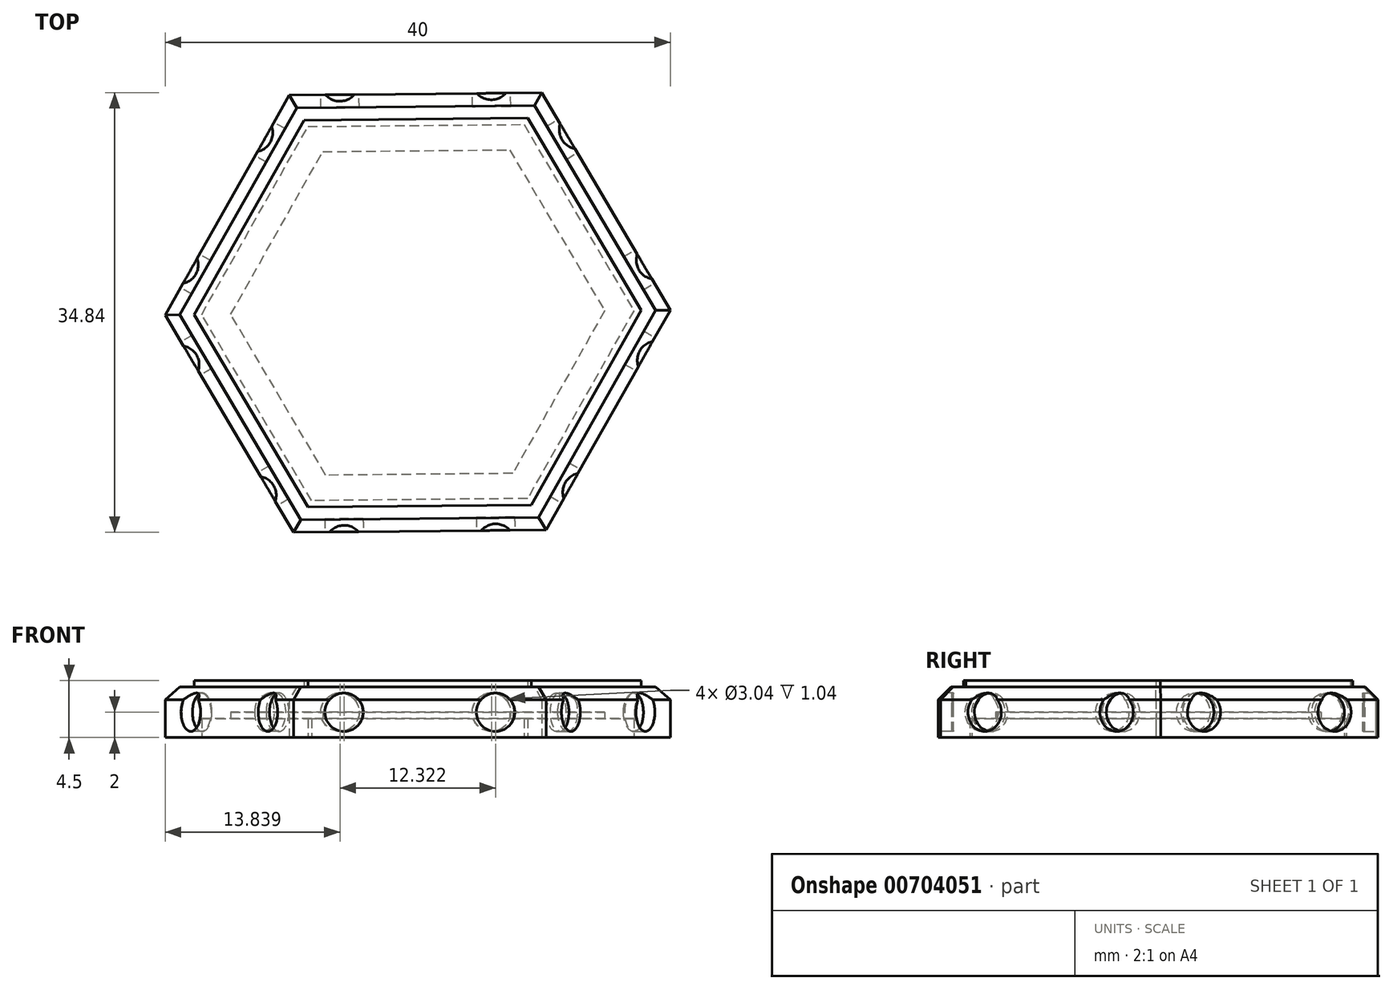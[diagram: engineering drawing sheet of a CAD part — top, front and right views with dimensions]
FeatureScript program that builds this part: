
annotation { "Feature Type Name" : "Feature", "Feature Type Description" : "" }
export const myFeature = defineFeature(function(context is Context, id is Id, definition is map)
    precondition{}
    {
        {
            var Q0;
            Q0=qCreatedBy(makeId("Top.planeOp"),FACE);
            var sketch = newSketch(context, id + "F0", { "sketchPlane" : qUnion([Q0])});
            skCircle(sketch, "E0.cCircle", {"center": v(0, 0) * mm, "radius": 15.32 * mm, "construction": true});
            skLineSegment(sketch, "E0.0", {"start": v(-17.69, -0.17) * mm, "end": v(-9, 15.23) * mm});
            skLineSegment(sketch, "E0.1", {"start": v(-9, 15.23) * mm, "end": v(8.7, 15.4) * mm});
            skLineSegment(sketch, "E0.2", {"start": v(8.7, 15.4) * mm, "end": v(17.69, 0.17) * mm});
            skLineSegment(sketch, "E0.3", {"start": v(17.69, 0.17) * mm, "end": v(9, -15.23) * mm});
            skLineSegment(sketch, "E0.4", {"start": v(9, -15.23) * mm, "end": v(-8.7, -15.4) * mm});
            skLineSegment(sketch, "E0.5", {"start": v(-8.7, -15.4) * mm, "end": v(-17.69, -0.17) * mm});
            skPoint(sketch, "E0.0.midPoint", {"position": v(-13.34, 7.53) * mm});
            skLineSegment(sketch, "E1.0", {"start": v(-9.83, -17.42) * mm, "end": v(-20, -0.2) * mm});
            skLineSegment(sketch, "E1.1", {"start": v(-10.17, 17.22) * mm, "end": v(9.83, 17.42) * mm});
            skLineSegment(sketch, "E1.2", {"start": v(9.83, 17.42) * mm, "end": v(20, 0.2) * mm});
            skLineSegment(sketch, "E1.3", {"start": v(-20, -0.2) * mm, "end": v(-10.17, 17.22) * mm});
            skLineSegment(sketch, "E1.4", {"start": v(20, 0.2) * mm, "end": v(10.17, -17.22) * mm});
            skLineSegment(sketch, "E1.5", {"start": v(10.17, -17.22) * mm, "end": v(-9.83, -17.42) * mm});
            skSolve(sketch);
        }
        {
            var Q0;
            Q0=makeQuery(id+"F0.imprint","IMPRINT",FACE,{"disambiguationData":[TD([[makeQuery(id+"F0.imprint","IMPRINT",EDGE,{"derivedFrom":sQuery(id+"F0.wireOp",EDGE,"E0.0")}),-1.0]])]});
            extrude(context, id + "F1", {"entities" : qUnion([Q0]), "depth" : 4.5 * mm, "offsetDistance" : 25 * mm});
        }
        {
            var Q0;
            Q0=makeQuery(id+"F0.imprint","IMPRINT",FACE,{"disambiguationData":[TD([[makeQuery(id+"F0.imprint","IMPRINT",EDGE,{"derivedFrom":sQuery(id+"F0.wireOp",EDGE,"E0.0")}),1.0]])]});
            extrude(context, id + "F2", {"entities" : qUnion([Q0]), "operationType" : NewBodyOperationType.ADD, "depth" : 4 * mm, "offsetDistance" : 25 * mm});
        }
        {
            var Q0;
            {var subQ0=sQuery(id+"F0.wireOp",EDGE,"E0.5");var subQ1=sQuery(id+"F0.wireOp",EDGE,"E0.4");var subQ2=sQuery(id+"F0.wireOp",EDGE,"E0.3");var subQ3=sQuery(id+"F0.wireOp",EDGE,"E0.2");var subQ4=sQuery(id+"F0.wireOp",EDGE,"E0.1");var subQ5=sQuery(id+"F0.wireOp",EDGE,"E0.0");Q0=makeQuery(id+"F2.boolean.opBoolean","MERGE",FACE,{"derivedFrom":[makeQuery(id+"F1.opExtrude","CAP_FACE",FACE,{"disambiguationData":[OSD([subQ5,subQ4,subQ3,subQ2,subQ1,subQ0])],"isStart":true}),makeQuery(id+"F2.opExtrude","CAP_FACE",FACE,{"disambiguationData":[OSD([subQ5,subQ4,subQ3,subQ2,subQ1,subQ0,sQuery(id+"F0.wireOp",EDGE,"E1.0"),sQuery(id+"F0.wireOp",EDGE,"E1.1"),sQuery(id+"F0.wireOp",EDGE,"E1.2"),sQuery(id+"F0.wireOp",EDGE,"E1.3"),sQuery(id+"F0.wireOp",EDGE,"E1.4"),sQuery(id+"F0.wireOp",EDGE,"E1.5")])],"isStart":true})]});}
            shell(context, id + "F3", {"entities" : qUnion([Q0]), "thickness" : 2.5 * mm});
        }
        {
            var Q0;
            Q0=makeQuery(id+"F2.opExtrude","SWEPT_FACE",FACE,{"disambiguationData":[OSD([sQuery(id+"F0.wireOp",EDGE,"E1.4")])]});
            var sketch = newSketch(context, id + "F4", { "sketchPlane" : qUnion([Q0])});
            skCircle(sketch, "E2", {"center": v(6, 2) * mm, "radius": 1.52 * mm});
            skCircle(sketch, "E3", {"center": v(-6, 2) * mm, "radius": 1.52 * mm});
            skSolve(sketch);
        }
        {
            var Q0;
            Q0=makeQuery(id+"F4.imprint","IMPRINT",FACE,{"disambiguationData":[TD([[makeQuery(id+"F4.imprint","IMPRINT",EDGE,{"derivedFrom":sQuery(id+"F4.wireOp",EDGE,"E3")}),1.0]])]});
            var Q1;
            Q1=makeQuery(id+"F4.imprint","IMPRINT",FACE,{"disambiguationData":[TD([[makeQuery(id+"F4.imprint","IMPRINT",EDGE,{"derivedFrom":sQuery(id+"F4.wireOp",EDGE,"E2")}),1.0]])]});
            extrude(context, id + "F5", {"entities" : qUnion([Q0, Q1]), "operationType" : NewBodyOperationType.REMOVE, "oppositeDirection" : true, "depth" : 1.04 * mm, "offsetDistance" : 25 * mm});
        }
        {
            var Q0;
            Q0=makeQuery(id+"F2.opExtrude","SWEPT_FACE",FACE,{"disambiguationData":[OSD([sQuery(id+"F0.wireOp",EDGE,"E1.5")])]});
            var sketch = newSketch(context, id + "F6", { "sketchPlane" : qUnion([Q0])});
            skCircle(sketch, "E4", {"center": v(-6, 2) * mm, "radius": 1.52 * mm});
            skCircle(sketch, "E5", {"center": v(6, 2) * mm, "radius": 1.52 * mm});
            skSolve(sketch);
        }
        {
            var Q0;
            Q0 = qSketchRegion(id + "F6", true);
            extrude(context, id + "F7", {"entities" : qUnion([Q0]), "operationType" : NewBodyOperationType.REMOVE, "oppositeDirection" : true, "depth" : 1.04 * mm, "offsetDistance" : 25 * mm});
        }
        {
            var Q0;
            Q0=makeQuery(id+"F2.opExtrude","SWEPT_FACE",FACE,{"disambiguationData":[OSD([sQuery(id+"F0.wireOp",EDGE,"E1.0")])]});
            var sketch = newSketch(context, id + "F8", { "sketchPlane" : qUnion([Q0])});
            skCircle(sketch, "E6", {"center": v(-6, 2) * mm, "radius": 1.52 * mm});
            skCircle(sketch, "E7", {"center": v(6, 2) * mm, "radius": 1.52 * mm});
            skSolve(sketch);
        }
        {
            var Q0;
            Q0 = qSketchRegion(id + "F8", true);
            extrude(context, id + "F9", {"entities" : qUnion([Q0]), "operationType" : NewBodyOperationType.REMOVE, "oppositeDirection" : true, "depth" : 1.04 * mm, "offsetDistance" : 25 * mm});
        }
        {
            var Q0;
            Q0=makeQuery(id+"F2.opExtrude","SWEPT_FACE",FACE,{"disambiguationData":[OSD([sQuery(id+"F0.wireOp",EDGE,"E1.3")])]});
            var sketch = newSketch(context, id + "F10", { "sketchPlane" : qUnion([Q0])});
            skCircle(sketch, "E8", {"center": v(-6, 2) * mm, "radius": 1.52 * mm});
            skCircle(sketch, "E9", {"center": v(6, 2) * mm, "radius": 1.52 * mm});
            skSolve(sketch);
        }
        {
            var Q0;
            Q0 = qSketchRegion(id + "F10", true);
            extrude(context, id + "F11", {"entities" : qUnion([Q0]), "operationType" : NewBodyOperationType.REMOVE, "oppositeDirection" : true, "depth" : 1.04 * mm, "offsetDistance" : 25 * mm});
        }
        {
            var Q0;
            Q0=makeQuery(id+"F2.opExtrude","SWEPT_FACE",FACE,{"disambiguationData":[OSD([sQuery(id+"F0.wireOp",EDGE,"E1.1")])]});
            var sketch = newSketch(context, id + "F12", { "sketchPlane" : qUnion([Q0])});
            skCircle(sketch, "E10", {"center": v(-6, 2) * mm, "radius": 1.52 * mm});
            skPoint(sketch, "E10.centerSnap0", {"position": v(-10, 2) * mm});
            skCircle(sketch, "E11", {"center": v(6, 2) * mm, "radius": 1.52 * mm});
            skSolve(sketch);
        }
        {
            var Q0;
            Q0 = qSketchRegion(id + "F12", true);
            extrude(context, id + "F13", {"entities" : qUnion([Q0]), "operationType" : NewBodyOperationType.REMOVE, "oppositeDirection" : true, "depth" : 1.04 * mm, "offsetDistance" : 25 * mm});
        }
        {
            var Q0;
            Q0=makeQuery(id+"F2.opExtrude","SWEPT_FACE",FACE,{"disambiguationData":[OSD([sQuery(id+"F0.wireOp",EDGE,"E1.2")])]});
            var sketch = newSketch(context, id + "F14", { "sketchPlane" : qUnion([Q0])});
            skCircle(sketch, "E12", {"center": v(-6, 2) * mm, "radius": 1.52 * mm});
            skCircle(sketch, "E13", {"center": v(6, 2) * mm, "radius": 1.52 * mm});
            skSolve(sketch);
        }
        {
            var Q0;
            Q0 = qSketchRegion(id + "F14", true);
            extrude(context, id + "F15", {"entities" : qUnion([Q0]), "operationType" : NewBodyOperationType.REMOVE, "oppositeDirection" : true, "depth" : 1.04 * mm, "offsetDistance" : 25 * mm});
        }
        {
            var Q0;
            Q0=makeQuery(id+"F2.opExtrude","CAP_EDGE",EDGE,{"disambiguationData":[OSD([sQuery(id+"F0.wireOp",EDGE,"E1.2")])],"isStart":false});
            var Q1;
            Q1=makeQuery(id+"F2.opExtrude","CAP_EDGE",EDGE,{"disambiguationData":[OSD([sQuery(id+"F0.wireOp",EDGE,"E1.4")])],"isStart":false});
            var Q2;
            Q2=makeQuery(id+"F2.opExtrude","CAP_EDGE",EDGE,{"disambiguationData":[OSD([sQuery(id+"F0.wireOp",EDGE,"E1.5")])],"isStart":false});
            var Q3;
            Q3=makeQuery(id+"F2.opExtrude","CAP_EDGE",EDGE,{"disambiguationData":[OSD([sQuery(id+"F0.wireOp",EDGE,"E1.0")])],"isStart":false});
            var Q4;
            Q4=makeQuery(id+"F2.opExtrude","CAP_EDGE",EDGE,{"disambiguationData":[OSD([sQuery(id+"F0.wireOp",EDGE,"E1.3")])],"isStart":false});
            var Q5;
            Q5=makeQuery(id+"F2.opExtrude","CAP_EDGE",EDGE,{"disambiguationData":[OSD([sQuery(id+"F0.wireOp",EDGE,"E1.1")])],"isStart":false});
            chamfer(context, id + "F16", {"entities" : qUnion([Q0, Q1, Q2, Q3, Q4, Q5]), "width" : 1 * mm, "tangentPropagation" : true});
        }
    });
